# Revit family: Toilet_Seat-Elongated_Closed_Front-KOHLER-Kathryn-K-4701
name_source: partatom
category: Specialty Equipment
revit_build: Autodesk Revit 2015 (Build: 20140606_1530(x64)
units: mm (PartAtom-declared; Revit-internal decimal feet)

## types (16) — shared parameters
ADA Compliant = No
Assembly Code = C1030200
Date Modified = 05/30/2019
Default Elevation = 0"
Height = 1 1/16"
Length = 18 5/8"
Manufacturer = KOHLER Co.
MasterFormat 1995 = 10820
MasterFormat 2004 = 10.28.13
Material = Molded Wood
Product Documentation Link = https://www.us.kohler.com
Product Name = Kathryn
Product Page URL = http://www.us.kohler.com
URL = https://www.us.kohler.com
WaterSense Certified = No
Width = 14 5/8"

## per-type parameters (varying)
| type | Description | Finish | Hinges Finish | Model | Type |
| Vibrant Gold Hinges-AF,0-White | Elongated toilet seat with Vibrant French Gold hinges | Kohler-Wood-Molded-0-White | Kohler-Metal-AF-Vibrant_French_Gold | K-4701-AF-0 | 1 |
| Vibrant Gold Hinges-AF,96-Biscuit | Elongated toilet seat with Vibrant French Gold hinges | Kohler-Wood-Molded-96-Biscuit | Kohler-Metal-AF-Vibrant_French_Gold | K-4701-AF-96 | 2 |
| Vibrant Gold Hinges-AF,NY-Dune | Elongated toilet seat with Vibrant French Gold hinges | Kohler-Wood-Molded-NY-Dune | Kohler-Metal-AF-Vibrant_French_Gold | K-4701-AF-NY | 3 |
| Vibrant Gold Hinges-AF,7-Black Black | Elongated toilet seat with Vibrant French Gold hinges | Kohler-Wood-Molded-7-Black_Black | Kohler-Metal-AF-Vibrant_French_Gold | K-4701-AF-7 | 4 |
| Vibrant Brushed Nickel Hinges-BN,0-White | Elongated toilet seat with Vibrant Brushed Nickel hinges | Kohler-Wood-Molded-0-White | Kohler-Metal-BN-Vibrant_Brushed_Nickel | K-4701-BN-0 | 5 |
| Vibrant Brushed Nickel Hinges-BN,96-Biscuit | Elongated toilet seat with Vibrant Brushed Nickel hinges | Kohler-Wood-Molded-96-Biscuit | Kohler-Metal-BN-Vibrant_Brushed_Nickel | K-4701-BN-96 | 6 |
| Vibrant Brushed Nickel Hinges-BN,NY-Dune | Elongated toilet seat with Vibrant Brushed Nickel hinges | Kohler-Wood-Molded-NY-Dune | Kohler-Metal-BN-Vibrant_Brushed_Nickel | K-4701-BN-NY | 7 |
| Vibrant Brushed Nickel Hinges-BN,7-Black Black | Elongated toilet seat with Vibrant Brushed Nickel hinges | Kohler-Wood-Molded-7-Black_Black | Kohler-Metal-BN-Vibrant_Brushed_Nickel | K-4701-BN-7 | 8 |
| Polished Chrome Hinges-CP,0-White | Elongated toilet seat with Polished Chrome hinges | Kohler-Wood-Molded-0-White | Kohler-Metal-CP-Polished_Chrome | K-4701-CP-0 | 9 |
| Polished Chrome Hinges-CP,96-Biscuit | Elongated toilet seat with Polished Chrome hinges | Kohler-Wood-Molded-96-Biscuit | Kohler-Metal-CP-Polished_Chrome | K-4701-CP-96 | 10 |
| Polished Chrome Hinges-CP,NY-Dune | Elongated toilet seat with Polished Chrome hinges | Kohler-Wood-Molded-NY-Dune | Kohler-Metal-CP-Polished_Chrome | K-4701-CP-NY | 11 |
| Polished Chrome Hinges-CP,7-Black Black | Elongated toilet seat with Polished Chrome hinges | Kohler-Wood-Molded-7-Black_Black | Kohler-Metal-CP-Polished_Chrome | K-4701-CP-7 | 12 |
| Vibrant Polished Nickel Hinges-SN,0-White | Elongated toilet seat with Vibrant Polished Nickel hinges | Kohler-Wood-Molded-0-White | Kohler-Metal-SN-Vibrant_Polished_Nickel | K-4701-SN-0 | 13 |
| Vibrant Polished Nickel Hinges-SN,96-Biscuit | Elongated toilet seat with Vibrant Polished Nickel hinges | Kohler-Wood-Molded-96-Biscuit | Kohler-Metal-SN-Vibrant_Polished_Nickel | K-4701-SN-96 | 14 |
| Vibrant Polished Nickel Hinges-SN,NY-Dune | Elongated toilet seat with Vibrant Polished Nickel hinges | Kohler-Wood-Molded-NY-Dune | Kohler-Metal-SN-Vibrant_Polished_Nickel | K-4701-SN-NY | 15 |
| Vibrant Polished Nickel Hinges-SN,7-Black Black | Elongated toilet seat with Vibrant Polished Nickel hinges | Kohler-Wood-Molded-7-Black_Black | Kohler-Metal-SN-Vibrant_Polished_Nickel | K-4701-SN-7 | 16 |

## geometry (parser evidence)
native form markers: Sweep x5
no freeform markers — native parametric forms only
